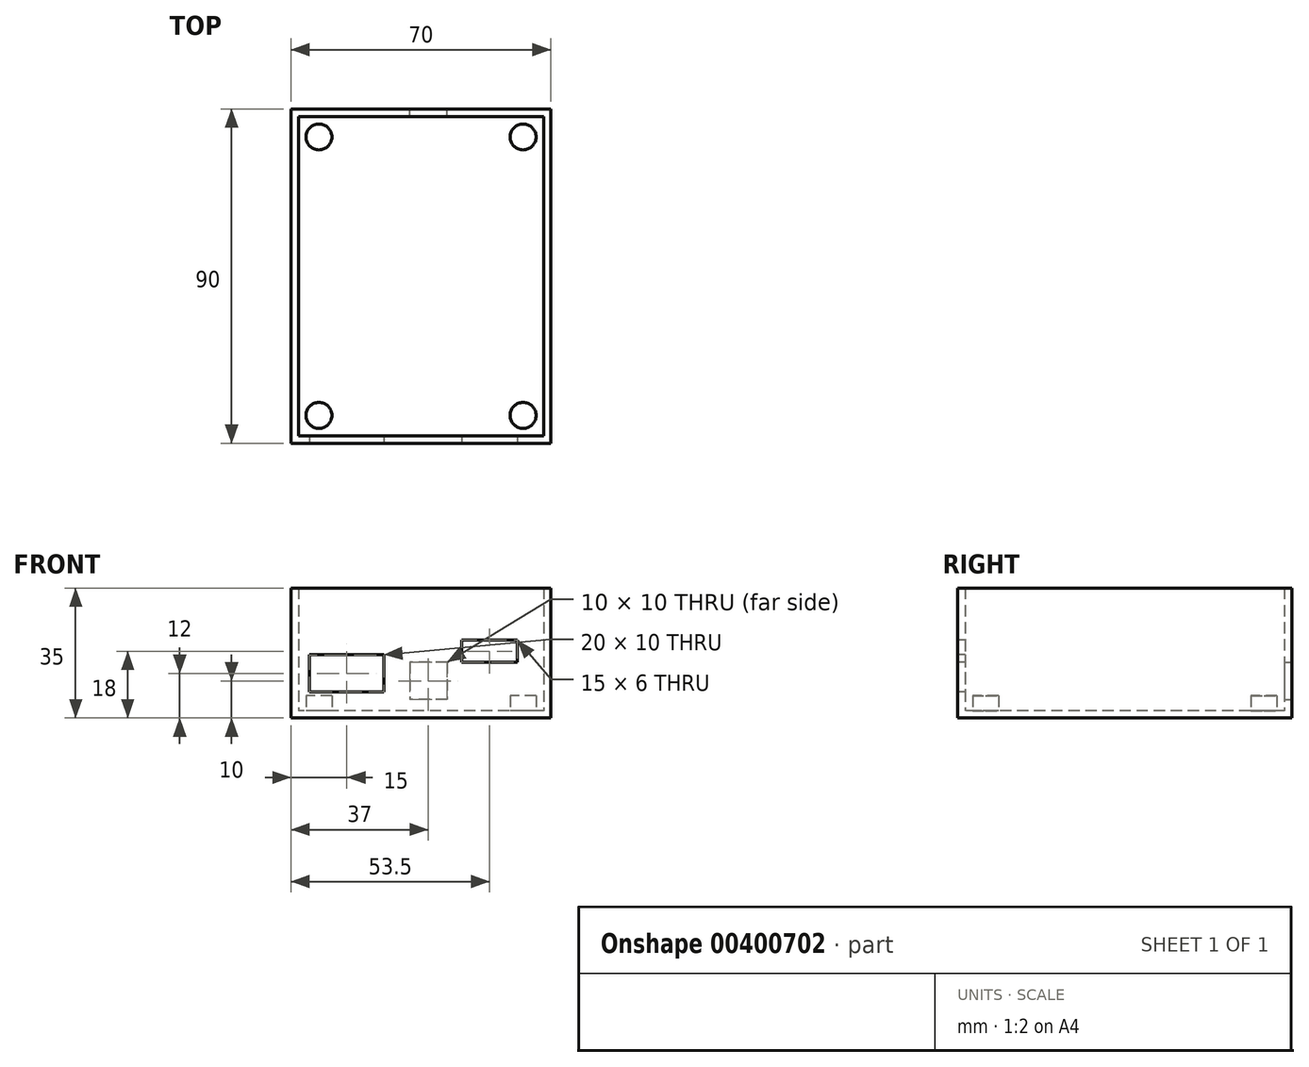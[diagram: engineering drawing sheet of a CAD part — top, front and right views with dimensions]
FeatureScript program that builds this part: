
annotation { "Feature Type Name" : "Feature", "Feature Type Description" : "" }
export const myFeature = defineFeature(function(context is Context, id is Id, definition is map)
    precondition{}
    {
        {
            var Q0;
            Q0=qCreatedBy(makeId("Top.planeOp"),FACE);
            var sketch = newSketch(context, id + "F0", { "sketchPlane" : qUnion([Q0])});
            skLineSegment(sketch, "E0.bottom", {"start": v(35, 45) * mm, "end": v(-35, 45) * mm});
            skLineSegment(sketch, "E0.top", {"start": v(35, -45) * mm, "end": v(-35, -45) * mm});
            skLineSegment(sketch, "E0.left", {"start": v(35, 45) * mm, "end": v(35, -45) * mm});
            skLineSegment(sketch, "E0.right", {"start": v(-35, 45) * mm, "end": v(-35, -45) * mm});
            skPoint(sketch, "E0.middle", {"position": v(0, 0) * mm});
            skSolve(sketch);
        }
        {
            var Q0;
            Q0=makeQuery(id+"F0.imprint","IMPRINT",FACE,{"disambiguationData":[TD([[makeQuery(id+"F0.imprint","IMPRINT",EDGE,{"derivedFrom":sQuery(id+"F0.wireOp",EDGE,"E0.bottom")}),1.0]])]});
            extrude(context, id + "F1", {"entities" : qUnion([Q0]), "depth" : 35 * mm});
        }
        {
            var Q0;
            Q0=makeQuery(id+"F1.opExtrude","CAP_FACE",FACE,{"disambiguationData":[OSD([sQuery(id+"F0.wireOp",EDGE,"E0.bottom"),sQuery(id+"F0.wireOp",EDGE,"E0.top"),sQuery(id+"F0.wireOp",EDGE,"E0.left"),sQuery(id+"F0.wireOp",EDGE,"E0.right")])],"isStart":false});
            shell(context, id + "F2", {"entities" : qUnion([Q0]), "thickness" : 2 * mm});
        }
        {
            var Q0;
            Q0=makeQuery(id+"F2.opShell","OFFSET_FACE",FACE,{"disambiguationData":[OSD([sQuery(id+"F0.wireOp",EDGE,"E0.bottom"),sQuery(id+"F0.wireOp",EDGE,"E0.top"),sQuery(id+"F0.wireOp",EDGE,"E0.left"),sQuery(id+"F0.wireOp",EDGE,"E0.right")])]});
            var sketch = newSketch(context, id + "F3", { "sketchPlane" : qUnion([Q0])});
            skLineSegment(sketch, "E1.bottom", {"start": v(27.5, 37.5) * mm, "end": v(-27.5, 37.5) * mm, "construction": true});
            skLineSegment(sketch, "E1.top", {"start": v(27.5, -37.5) * mm, "end": v(-27.5, -37.5) * mm, "construction": true});
            skLineSegment(sketch, "E1.left", {"start": v(27.5, 37.5) * mm, "end": v(27.5, -37.5) * mm, "construction": true});
            skLineSegment(sketch, "E1.right", {"start": v(-27.5, 37.5) * mm, "end": v(-27.5, -37.5) * mm, "construction": true});
            skPoint(sketch, "E1.middle", {"position": v(0, 0) * mm});
            skCircle(sketch, "E2", {"center": v(-27.5, 37.5) * mm, "radius": 3.5 * mm});
            skCircle(sketch, "E3", {"center": v(27.5, 37.5) * mm, "radius": 3.5 * mm});
            skCircle(sketch, "E4", {"center": v(-27.5, -37.5) * mm, "radius": 3.5 * mm});
            skCircle(sketch, "E5", {"center": v(27.5, -37.5) * mm, "radius": 3.5 * mm});
            skSolve(sketch);
        }
        {
            var Q0;
            Q0=makeQuery(id+"F3.imprint","IMPRINT",FACE,{"disambiguationData":[TD([[makeQuery(id+"F3.imprint","IMPRINT",EDGE,{"derivedFrom":sQuery(id+"F3.wireOp",EDGE,"E2")}),1.0]])]});
            var Q1;
            Q1=makeQuery(id+"F3.imprint","IMPRINT",FACE,{"disambiguationData":[TD([[makeQuery(id+"F3.imprint","IMPRINT",EDGE,{"derivedFrom":sQuery(id+"F3.wireOp",EDGE,"E5")}),1.0]])]});
            var Q2;
            Q2=makeQuery(id+"F3.imprint","IMPRINT",FACE,{"disambiguationData":[TD([[makeQuery(id+"F3.imprint","IMPRINT",EDGE,{"derivedFrom":sQuery(id+"F3.wireOp",EDGE,"E3")}),1.0]])]});
            var Q3;
            Q3=makeQuery(id+"F3.imprint","IMPRINT",FACE,{"disambiguationData":[TD([[makeQuery(id+"F3.imprint","IMPRINT",EDGE,{"derivedFrom":sQuery(id+"F3.wireOp",EDGE,"E4")}),1.0]])]});
            extrude(context, id + "F4", {"entities" : qUnion([Q0, Q1, Q2, Q3]), "operationType" : NewBodyOperationType.ADD, "depth" : 4 * mm});
        }
        {
            var Q0;
            Q0=makeQuery(id+"F1.opExtrude","SWEPT_FACE",FACE,{"disambiguationData":[OSD([sQuery(id+"F0.wireOp",EDGE,"E0.top")])]});
            var sketch = newSketch(context, id + "F5", { "sketchPlane" : qUnion([Q0])});
            skLineSegment(sketch, "E6.bottom", {"start": v(33, 33) * mm, "end": v(-33, 33) * mm, "construction": true});
            skLineSegment(sketch, "E6.top", {"start": v(33, 2) * mm, "end": v(-33, 2) * mm, "construction": true});
            skLineSegment(sketch, "E6.left", {"start": v(33, 33) * mm, "end": v(33, 2) * mm, "construction": true});
            skLineSegment(sketch, "E6.right", {"start": v(-33, 33) * mm, "end": v(-33, 2) * mm, "construction": true});
            skPoint(sketch, "E6.middle", {"position": v(0, 17.5) * mm});
            skLineSegment(sketch, "E7", {"start": v(0, 2) * mm, "end": v(0, 7) * mm, "construction": true});
            skLineSegment(sketch, "E8", {"start": v(0, 7) * mm, "end": v(30, 7) * mm, "construction": true});
            skLineSegment(sketch, "E9", {"start": v(0, 7) * mm, "end": v(-30, 7) * mm, "construction": true});
            skLineSegment(sketch, "E10.bottom", {"start": v(-30, 7) * mm, "end": v(-10, 7) * mm});
            skLineSegment(sketch, "E10.top", {"start": v(-30, 17) * mm, "end": v(-10, 17) * mm});
            skLineSegment(sketch, "E10.left", {"start": v(-30, 7) * mm, "end": v(-30, 17) * mm});
            skLineSegment(sketch, "E10.right", {"start": v(-10, 7) * mm, "end": v(-10, 17) * mm});
            skLineSegment(sketch, "E11", {"start": v(30, 7) * mm, "end": v(30, 15) * mm, "construction": true});
            skLineSegment(sketch, "E12", {"start": v(30, 15) * mm, "end": v(26, 15) * mm, "construction": true});
            skLineSegment(sketch, "E13.bottom", {"start": v(26, 15) * mm, "end": v(11, 15) * mm});
            skLineSegment(sketch, "E13.top", {"start": v(26, 21) * mm, "end": v(11, 21) * mm});
            skLineSegment(sketch, "E13.left", {"start": v(26, 15) * mm, "end": v(26, 21) * mm});
            skLineSegment(sketch, "E13.right", {"start": v(11, 15) * mm, "end": v(11, 21) * mm});
            skSolve(sketch);
        }
        {
            var Q0;
            Q0=makeQuery(id+"F5.imprint","IMPRINT",FACE,{"disambiguationData":[TD([[makeQuery(id+"F5.imprint","IMPRINT",EDGE,{"derivedFrom":sQuery(id+"F5.wireOp",EDGE,"E10.bottom")}),1.0]])]});
            var Q1;
            Q1=makeQuery(id+"F5.imprint","IMPRINT",FACE,{"disambiguationData":[TD([[makeQuery(id+"F5.imprint","IMPRINT",EDGE,{"derivedFrom":sQuery(id+"F5.wireOp",EDGE,"E13.bottom")}),-1.0]])]});
            extrude(context, id + "F6", {"entities" : qUnion([Q0, Q1]), "operationType" : NewBodyOperationType.REMOVE, "endBound" : BoundingType.UP_TO_NEXT, "oppositeDirection" : true, "depth" : 25 * mm});
        }
        {
            var Q0;
            Q0=makeQuery(id+"F1.opExtrude","SWEPT_FACE",FACE,{"disambiguationData":[OSD([sQuery(id+"F0.wireOp",EDGE,"E0.bottom")])]});
            var sketch = newSketch(context, id + "F7", { "sketchPlane" : qUnion([Q0])});
            skLineSegment(sketch, "E14", {"start": v(0, 0) * mm, "end": v(0, 5) * mm, "construction": true});
            skLineSegment(sketch, "E15", {"start": v(0, 5) * mm, "end": v(-30, 5) * mm, "construction": true});
            skLineSegment(sketch, "E16", {"start": v(-30, 5) * mm, "end": v(-30, 15) * mm, "construction": true});
            skLineSegment(sketch, "E17", {"start": v(-30, 15) * mm, "end": v(-7, 15) * mm, "construction": true});
            skLineSegment(sketch, "E18.bottom", {"start": v(-7, 15) * mm, "end": v(3, 15) * mm});
            skLineSegment(sketch, "E18.top", {"start": v(-7, 5) * mm, "end": v(3, 5) * mm});
            skLineSegment(sketch, "E18.left", {"start": v(-7, 15) * mm, "end": v(-7, 5) * mm});
            skLineSegment(sketch, "E18.right", {"start": v(3, 15) * mm, "end": v(3, 5) * mm});
            skSolve(sketch);
        }
        {
            var Q0;
            Q0=makeQuery(id+"F7.imprint","IMPRINT",FACE,{"disambiguationData":[TD([[makeQuery(id+"F7.imprint","IMPRINT",EDGE,{"derivedFrom":sQuery(id+"F7.wireOp",EDGE,"E18.bottom")}),-1.0]])]});
            extrude(context, id + "F8", {"entities" : qUnion([Q0]), "operationType" : NewBodyOperationType.REMOVE, "endBound" : BoundingType.UP_TO_NEXT, "oppositeDirection" : true, "depth" : 25 * mm});
        }
    });
